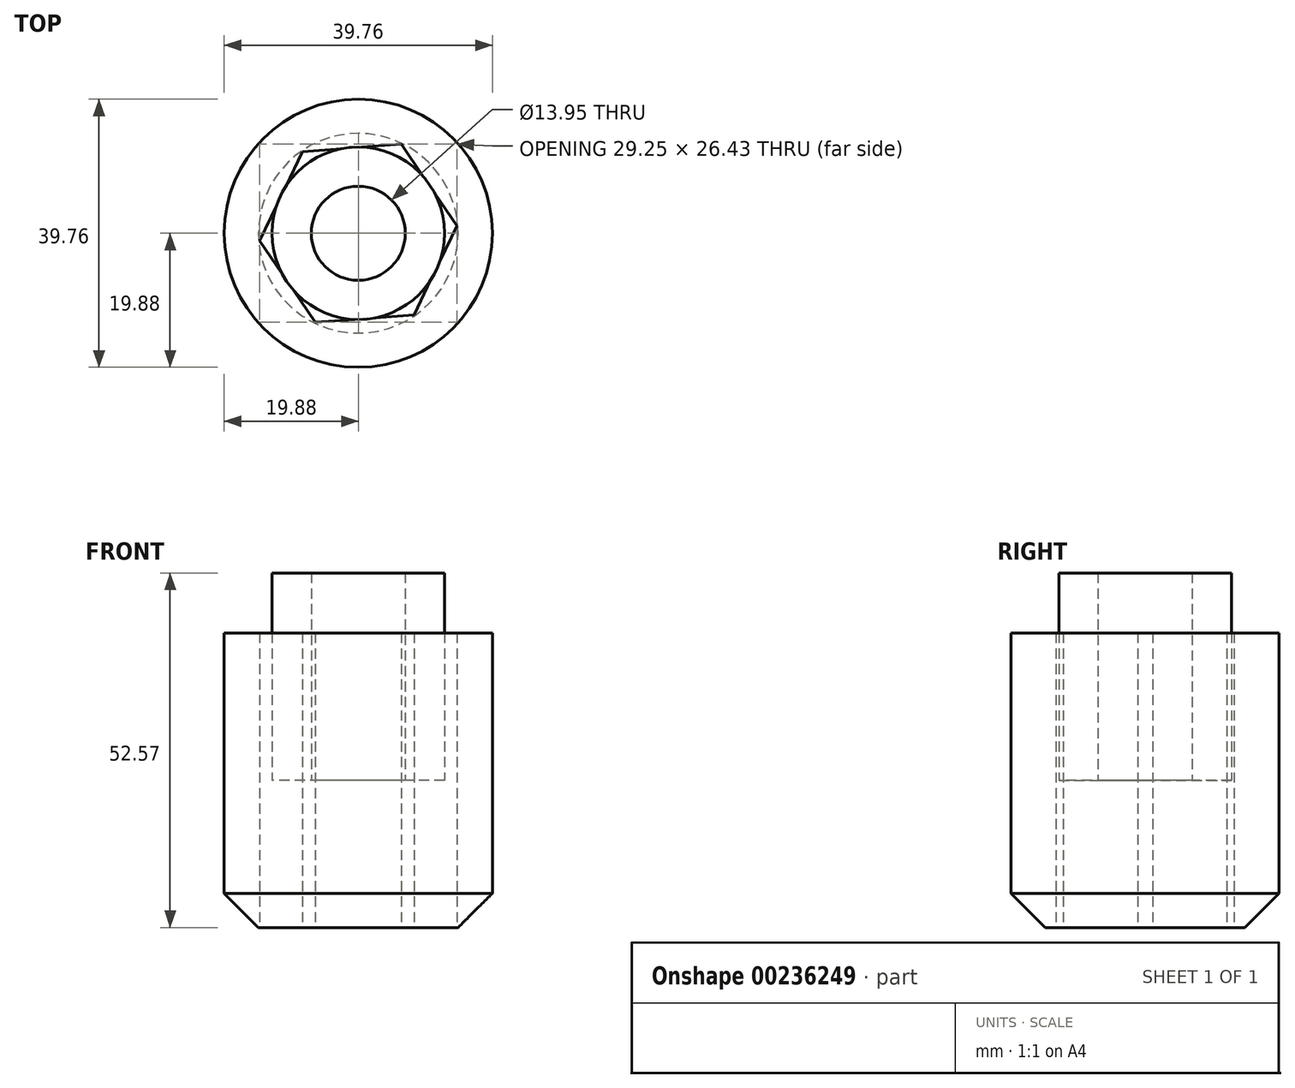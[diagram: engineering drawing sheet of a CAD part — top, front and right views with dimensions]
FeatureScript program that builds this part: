
annotation { "Feature Type Name" : "Feature", "Feature Type Description" : "" }
export const myFeature = defineFeature(function(context is Context, id is Id, definition is map)
    precondition{}
    {
        {
            var Q0;
            Q0=qCreatedBy(makeId("Top.planeOp"),FACE);
            var sketch = newSketch(context, id + "F0", { "sketchPlane" : qUnion([Q0])});
            skCircle(sketch, "E0", {"center": v(0, 0) * mm, "radius": 12.7 * mm});
            skCircle(sketch, "E1", {"center": v(0, 0) * mm, "radius": 19.88 * mm});
            skCircle(sketch, "E2.cCircle", {"center": v(0, 0) * mm, "radius": 12.7 * mm, "construction": true});
            skLineSegment(sketch, "E2.0", {"start": v(8.27, -12.11) * mm, "end": v(-6.36, -13.22) * mm});
            skLineSegment(sketch, "E2.1", {"start": v(-6.36, -13.22) * mm, "end": v(-14.62, -1.1) * mm});
            skLineSegment(sketch, "E2.2", {"start": v(-14.62, -1.1) * mm, "end": v(-8.27, 12.11) * mm});
            skLineSegment(sketch, "E2.3", {"start": v(-8.27, 12.11) * mm, "end": v(6.36, 13.22) * mm});
            skLineSegment(sketch, "E2.4", {"start": v(6.36, 13.22) * mm, "end": v(14.62, 1.1) * mm});
            skLineSegment(sketch, "E2.5", {"start": v(14.62, 1.1) * mm, "end": v(8.27, -12.11) * mm});
            skPoint(sketch, "E2.0.midPoint", {"position": v(0.95, -12.66) * mm});
            skSolve(sketch);
        }
        {
            var Q0;
            Q0 = qSketchRegion(id + "F0", true);
            extrude(context, id + "F1", {"entities" : qUnion([Q0]), "endBound" : BoundingType.SYMMETRIC, "depth" : 43.69 * mm});
        }
        {
            var Q0;
            Q0=makeQuery(id+"F1.opExtrude","CAP_EDGE",EDGE,{"disambiguationData":[OSD([sQuery(id+"F0.wireOp",EDGE,"E1")])],"isStart":true});
            chamfer(context, id + "F2", {"entities" : qUnion([Q0]), "width" : 5.08 * mm, "tangentPropagation" : true});
        }
        {
            var Q0;
            {var subQ0=sQuery(id+"F0.wireOp",EDGE,"E0");var subQ4=makeQuery(id+"F0.imprint","INTERSECT",VERTEX,{"derivedFrom":[subQ0,sQuery(id+"F0.wireOp",EDGE,"E2.3")]});Q0=makeQuery(id+"F0.imprint","IMPRINT",FACE,{"disambiguationData":[TD([[makeQuery(id+"F0.imprint","IMPRINT",EDGE,{"disambiguationData":[TD([[subQ4,1.0]])],"derivedFrom":subQ0}),1.0]])]});}
            var sketch = newSketch(context, id + "F3", { "sketchPlane" : qUnion([Q0])});
            skCircle(sketch, "E3", {"center": v(0, 0) * mm, "radius": 6.98 * mm});
            skSolve(sketch);
        }
        {
            var Q0;
            {var subQ0=sQuery(id+"F0.wireOp",EDGE,"E0");var subQ4=makeQuery(id+"F0.imprint","INTERSECT",VERTEX,{"derivedFrom":[subQ0,sQuery(id+"F0.wireOp",EDGE,"E2.3")]});Q0=makeQuery(id+"F0.imprint","IMPRINT",FACE,{"disambiguationData":[TD([[makeQuery(id+"F0.imprint","IMPRINT",EDGE,{"disambiguationData":[TD([[subQ4,1.0]])],"derivedFrom":subQ0}),1.0]])]});}
            var sketch = newSketch(context, id + "F4", { "sketchPlane" : qUnion([Q0])});
            skCircle(sketch, "E4", {"center": v(0, 0) * mm, "radius": 12.79 * mm});
            skSolve(sketch);
        }
        {
            var Q0;
            Q0 = qSketchRegion(id + "F4", true);
            extrude(context, id + "F5", {"entities" : qUnion([Q0]), "depth" : 30.73 * mm});
        }
        {
            var Q0;
            Q0 = qSketchRegion(id + "F3", true);
            extrude(context, id + "F6", {"entities" : qUnion([Q0]), "operationType" : NewBodyOperationType.REMOVE, "depth" : 48.77 * mm});
        }
    });
